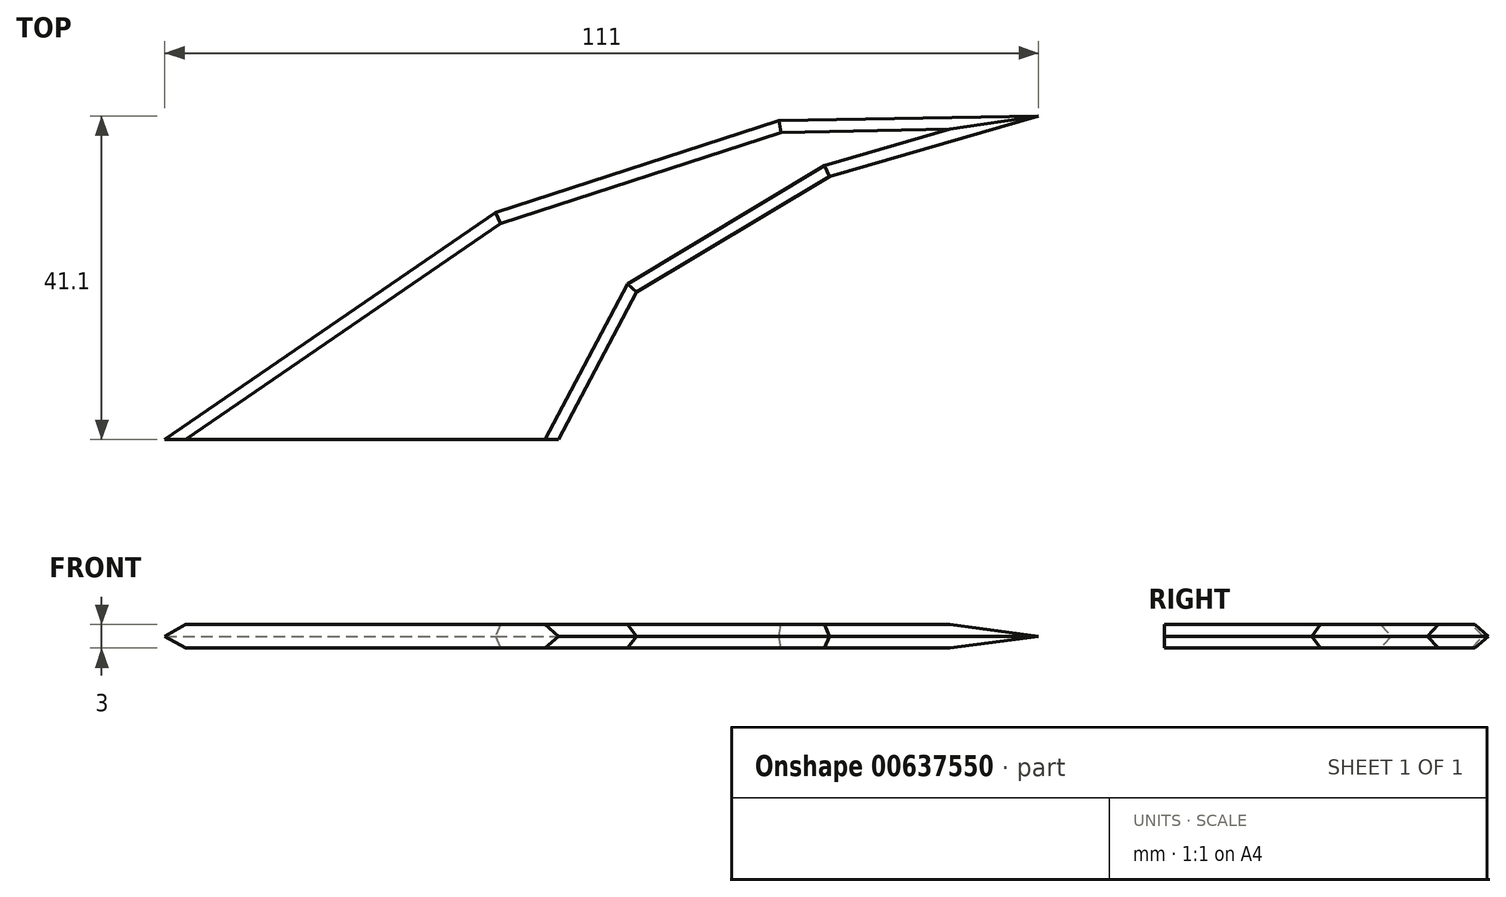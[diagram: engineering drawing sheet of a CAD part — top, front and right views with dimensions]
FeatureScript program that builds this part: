
annotation { "Feature Type Name" : "Feature", "Feature Type Description" : "" }
export const myFeature = defineFeature(function(context is Context, id is Id, definition is map)
    precondition{}
    {
        {
            var Q0;
            Q0=qCreatedBy(makeId("Top.planeOp"),FACE);
            var sketch = newSketch(context, id + "F0", { "sketchPlane" : qUnion([Q0])});
            skLineSegment(sketch, "E0", {"start": v(0, 0) * mm, "end": v(-50, 0) * mm});
            skLineSegment(sketch, "E1", {"start": v(-50, 0) * mm, "end": v(-8, 28.8) * mm});
            skLineSegment(sketch, "E2", {"start": v(-8, 28.8) * mm, "end": v(28, 40.5) * mm});
            skLineSegment(sketch, "E3", {"start": v(28, 40.5) * mm, "end": v(61, 41.1) * mm});
            skLineSegment(sketch, "E4", {"start": v(61, 41.1) * mm, "end": v(34.4, 33.4) * mm});
            skLineSegment(sketch, "E5", {"start": v(34.4, 33.4) * mm, "end": v(9.9, 18.7) * mm});
            skLineSegment(sketch, "E6", {"start": v(9.9, 18.7) * mm, "end": v(0, 0) * mm});
            skSolve(sketch);
        }
        {
            var Q0;
            Q0=makeQuery(id+"F0.imprint","IMPRINT",FACE,{"disambiguationData":[TD([[makeQuery(id+"F0.imprint","IMPRINT",EDGE,{"derivedFrom":sQuery(id+"F0.wireOp",EDGE,"E0")}),-1.0]])]});
            extrude(context, id + "F1", {"entities" : qUnion([Q0]), "depth" : 3 * mm, "offsetDistance" : 25 * mm});
        }
        {
            var Q0;
            Q0=makeQuery(id+"F1.opExtrude","CAP_EDGE",EDGE,{"disambiguationData":[OSD([sQuery(id+"F0.wireOp",EDGE,"E1")])],"isStart":false});
            var Q1;
            Q1=makeQuery(id+"F1.opExtrude","CAP_EDGE",EDGE,{"disambiguationData":[OSD([sQuery(id+"F0.wireOp",EDGE,"E2")])],"isStart":false});
            var Q2;
            Q2=makeQuery(id+"F1.opExtrude","CAP_EDGE",EDGE,{"disambiguationData":[OSD([sQuery(id+"F0.wireOp",EDGE,"E2")])],"isStart":true});
            var Q3;
            Q3=makeQuery(id+"F1.opExtrude","CAP_EDGE",EDGE,{"disambiguationData":[OSD([sQuery(id+"F0.wireOp",EDGE,"E1")])],"isStart":true});
            var Q4;
            Q4=makeQuery(id+"F1.opExtrude","CAP_EDGE",EDGE,{"disambiguationData":[OSD([sQuery(id+"F0.wireOp",EDGE,"E3")])],"isStart":true});
            var Q5;
            Q5=makeQuery(id+"F1.opExtrude","CAP_EDGE",EDGE,{"disambiguationData":[OSD([sQuery(id+"F0.wireOp",EDGE,"E3")])],"isStart":false});
            var Q6;
            Q6=makeQuery(id+"F1.opExtrude","CAP_EDGE",EDGE,{"disambiguationData":[OSD([sQuery(id+"F0.wireOp",EDGE,"E4")])],"isStart":false});
            var Q7;
            Q7=makeQuery(id+"F1.opExtrude","CAP_EDGE",EDGE,{"disambiguationData":[OSD([sQuery(id+"F0.wireOp",EDGE,"E4")])],"isStart":true});
            var Q8;
            Q8=makeQuery(id+"F1.opExtrude","CAP_EDGE",EDGE,{"disambiguationData":[OSD([sQuery(id+"F0.wireOp",EDGE,"E5")])],"isStart":false});
            var Q9;
            Q9=makeQuery(id+"F1.opExtrude","CAP_EDGE",EDGE,{"disambiguationData":[OSD([sQuery(id+"F0.wireOp",EDGE,"E5")])],"isStart":true});
            var Q10;
            Q10=makeQuery(id+"F1.opExtrude","CAP_EDGE",EDGE,{"disambiguationData":[OSD([sQuery(id+"F0.wireOp",EDGE,"E6")])],"isStart":false});
            var Q11;
            Q11=makeQuery(id+"F1.opExtrude","CAP_EDGE",EDGE,{"disambiguationData":[OSD([sQuery(id+"F0.wireOp",EDGE,"E6")])],"isStart":true});
            chamfer(context, id + "F2", {"entities" : qUnion([Q0, Q1, Q2, Q3, Q4, Q5, Q6, Q7, Q8, Q9, Q10, Q11]), "width" : 1.5 * mm, "tangentPropagation" : true});
        }
    });
